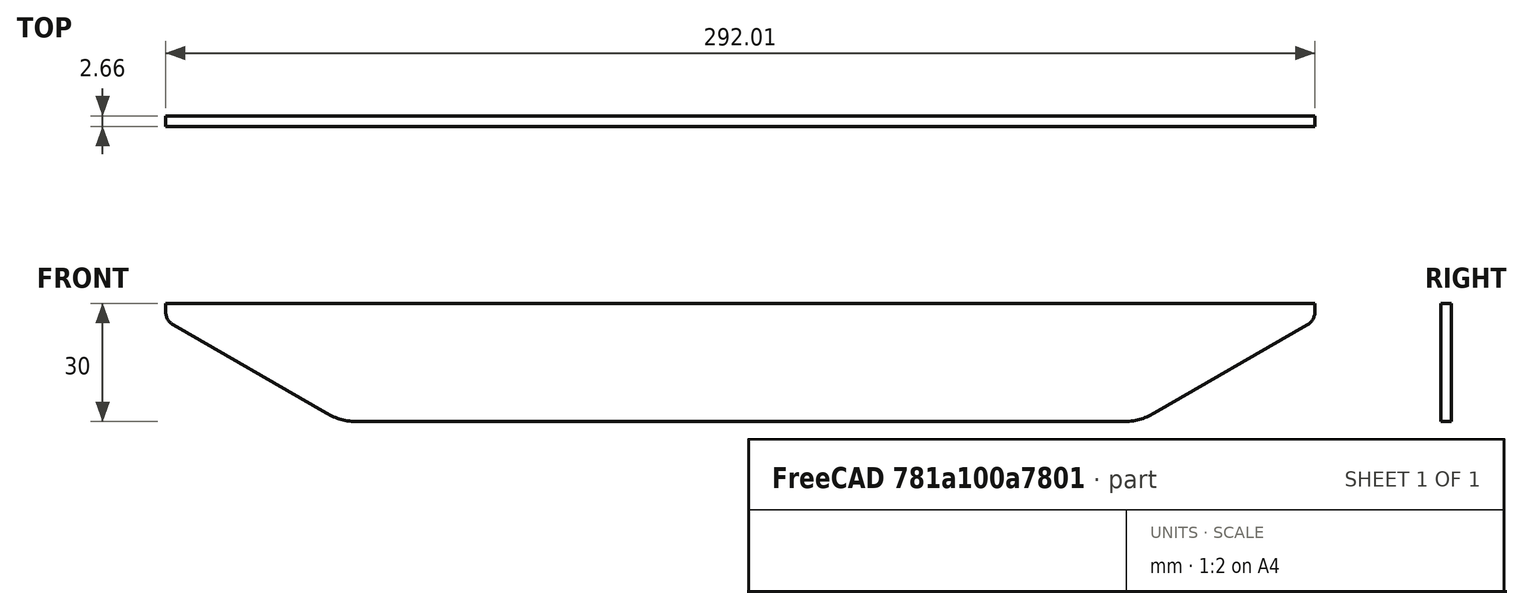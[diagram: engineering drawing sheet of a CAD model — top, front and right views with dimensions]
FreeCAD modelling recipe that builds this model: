
FCSTD DOCUMENT  (FreeCAD 0.20R29177 +426 (Git))
Label: DrivePlatformRib
License: All rights reserved
LicenseURL: http://en.wikipedia.org/wiki/All_rights_reserved
objects: App::DocumentObjectGroup×3, PartDesign::CoordinateSystem×1, App::FeaturePython×1, Sketcher::SketchObject×1, PartDesign::Pad×1, PartDesign::Body×1, App::Part×1, TechDraw::DrawSVGTemplate×1, TechDraw::DrawViewPart×1, TechDraw::DrawPage×1
note: 5 computed .brp shape members not serialized (recipe doc carries the construction recipe); baked Part::Feature solids carry a one-line shape summary decoded from their .brp
EXTERNAL_REF file=DrivePlatform.FCStd obj=Sketch_1
EXTERNAL_REF file=Params.FCStd obj=Spreadsheet

FEATURE [App::DocumentObjectGroup] Parts
FEATURE [PartDesign::CoordinateSystem] LCS_Origin
  AttacherType = Attacher::AttachEngine3D
  MapMode = 2
  Support = -> [X_Axis]
FEATURE [App::FeaturePython] Variables  # WARN: FeaturePython — macro-defined, semantics opaque (R4)
  Type = App::PropertyContainer
FEATURE [App::DocumentObjectGroup] Constraints
FEATURE [App::DocumentObjectGroup] Configurations
FEATURE [Sketcher::SketchObject] Sketch
  FullyConstrained = true
  MapMode = 5
  Placement = pos=(0,0,0) rot=(1,0,0;1.5708rad)
  Support = -> [XZ_Plane001]
  expr: Constraints[32] = <<DrivePlatform>>#<<Sketch_1>>.Constraints.BottomOffset
  expr: Constraints[33] = <<Params>>#<<Params>>.TableRollerDriveSupportRadius - 4
  sketch-geometry (14):
    g0: LineSegment StartX=-78.0112 StartY=0 StartZ=0 EndX=214 EndY=0 EndZ=0
    g1: LineSegment StartX=214 StartY=0 StartZ=0 EndX=214 EndY=-2 EndZ=0
    g2: LineSegment StartX=212 StartY=-5.4641 StartZ=0 EndX=173.215 EndY=-27.8564 EndZ=0
    g3: LineSegment StartX=165.215 StartY=-30 StartZ=0 EndX=-29.2266 EndY=-30 EndZ=0
    g4: LineSegment StartX=-37.2266 StartY=-27.8564 StartZ=0 EndX=-76.0112 EndY=-5.4641 EndZ=0
    g5: LineSegment StartX=-78.0112 StartY=-2 StartZ=0 EndX=-78.0112 EndY=0 EndZ=0
    g6: ArcOfCircle CenterX=210 CenterY=-2 CenterZ=0 NormalX=0 NormalY=0 NormalZ=1 AngleXU=0 Radius=4 StartAngle=5.23599 EndAngle=6.28319
    g7: GeomPoint X=214 Y=-4.3094 Z=0
    g8: ArcOfCircle CenterX=-74.0112 CenterY=-2 CenterZ=0 NormalX=0 NormalY=0 NormalZ=1 AngleXU=0 Radius=4 StartAngle=3.14159 EndAngle=4.18879
    g9: GeomPoint X=-78.0112 Y=-4.3094 Z=0
    g10: ArcOfCircle CenterX=-29.2266 CenterY=-14 CenterZ=0 NormalX=0 NormalY=0 NormalZ=1 AngleXU=0 Radius=16 StartAngle=4.18879 EndAngle=4.71239
    g11: GeomPoint X=-33.5137 Y=-30 Z=0
    g12: ArcOfCircle CenterX=165.215 CenterY=-14 CenterZ=0 NormalX=0 NormalY=0 NormalZ=1 AngleXU=0 Radius=16 StartAngle=4.71239 EndAngle=5.23599
    g13: GeomPoint X=169.503 Y=-30 Z=0
  constraints (34):
    c: PointOnObject(g0,g-1)
    c: PointOnObject(g0,g-1)
    c: Coincident(g0,g1)
    c: Vertical(g1)
    c: Horizontal(g3)
    c: Coincident(g5,g0)
    c: Vertical(g5)
    c: PointOnObject(g7,g1)
    c: PointOnObject(g7,g2)
    c: Tangent(g1,g6) = 1.5708
    c: Tangent(g2,g6) = 1.5708
    c: PointOnObject(g9,g4)
    c: PointOnObject(g9,g5)
    c: Tangent(g4,g8) = 1.5708
    c: Tangent(g5,g8) = 1.5708
    c: Equal(g6,g8)
    c: PointOnObject(g11,g3)
    c: PointOnObject(g11,g4)
    c: Tangent(g3,g10) = 1.5708
    c: Tangent(g4,g10) = 1.5708
    c: PointOnObject(g13,g3)
    c: PointOnObject(g13,g2)
    c: Tangent(g3,g12) = 1.5708
    c: Tangent(g2,g12) = 1.5708
    c: Equal(g12,g10)
    c: Radius(g6) = 4
    c: Radius(g12) = 16
    c: Equal(g5,g1)
    c: DistanceY(g1,g1) = 2
    c: DistanceY(g3,g-1) = 30
    c: Angle(g4,g0) = 0.523599
    c: Angle(g0,g2) = 0.523599
    c: DistanceX(g0,g-1) = 78.0112
    c: DistanceX(g-1,g0) = 214
FEATURE [PartDesign::Pad] Pad
  Direction = (0,-1,-2e-16)
  Length = 2.656
  Length2 = 10
  Midplane = true
  Placement = pos=(0,0,0) rot=(1,0,0;1.5708rad)
  Profile = -> Sketch
  ReferenceAxis = -> Sketch [N_Axis]
  Type = 0
  expr: Length = <<Params>>#<<Params>>.SheetMetalThickness
FEATURE [PartDesign::Body] Body
  Group = -> [Sketch,Pad]
  Origin = -> Origin001
  Tip = -> Pad
FEATURE [App::Part] Assembly
  AssemblyType = Part::Link
  Group = -> [LCS_Origin,Variables,Constraints,Configurations,Body]
  Origin = -> Origin
  Type = Assembly
FEATURE [TechDraw::DrawSVGTemplate] Template
  Height = 841
  Orientation = 1
  Width = 1189
FEATURE [TechDraw::DrawViewPart] View
  CoarseView = false
  Direction = (0,1,0)
  Focus = 100
  HardHidden = false
  IsoCount = 0
  IsoHidden = false
  IsoVisible = false
  LockPosition = false
  Perspective = false
  Rotation = 0
  ScaleType = 0
  SeamHidden = false
  SeamVisible = true
  SmoothHidden = false
  SmoothVisible = true
  Source = -> [Pad]
  X = 561.403
  XDirection = (0,0,-1)
  Y = 410.664
FEATURE [TechDraw::DrawPage] Page
  KeepUpdated = true
  NextBalloonIndex = 1
  ProjectionType = 0
  Template = -> Template
  Views = -> [View]
